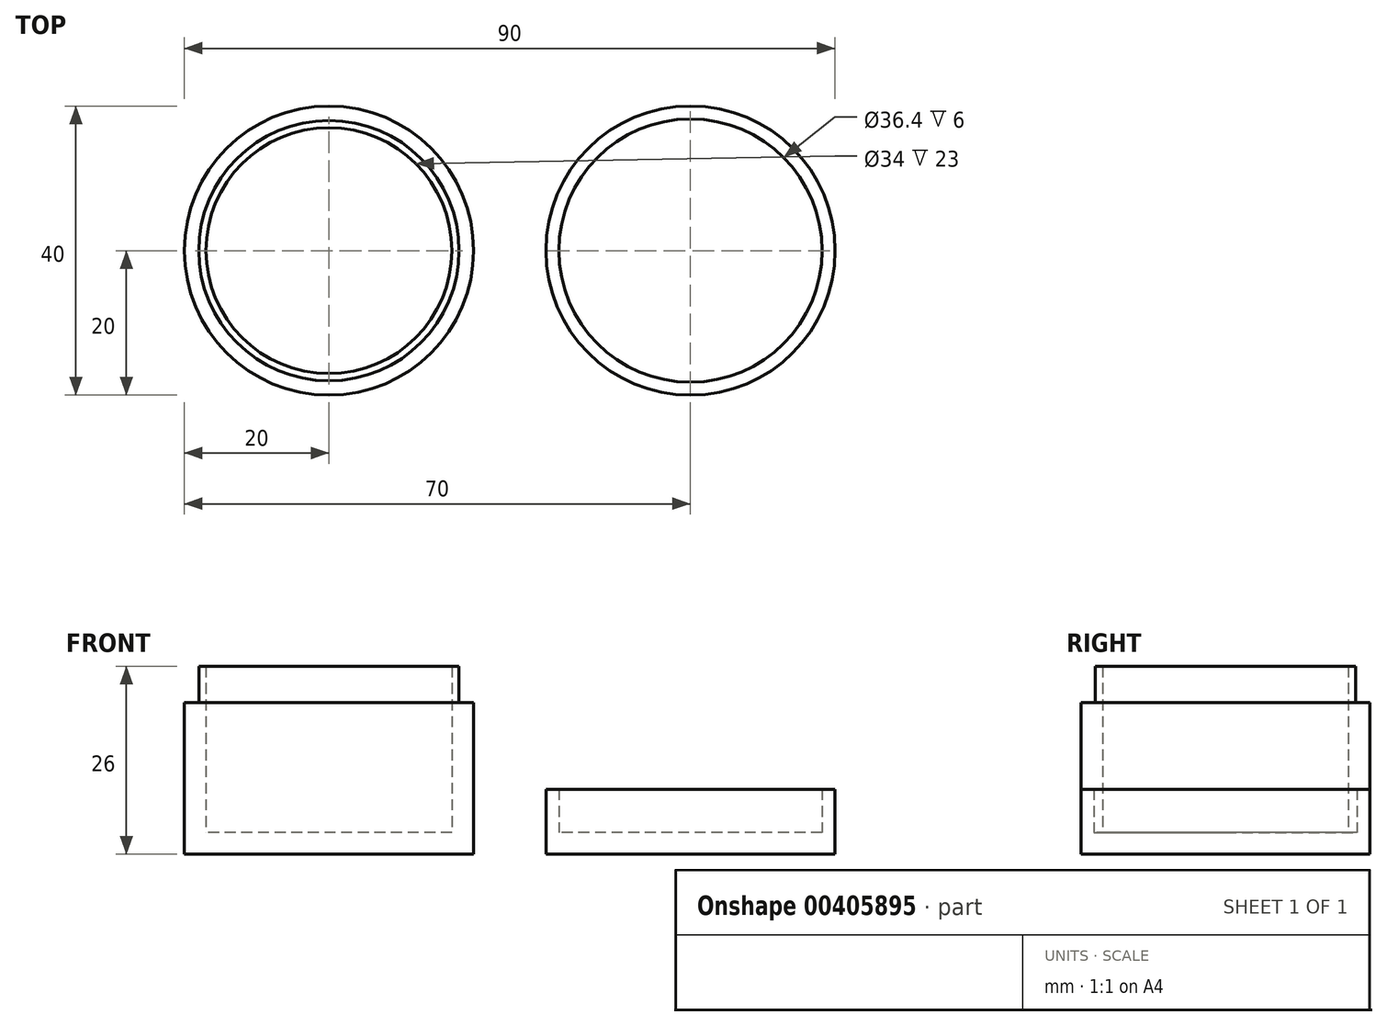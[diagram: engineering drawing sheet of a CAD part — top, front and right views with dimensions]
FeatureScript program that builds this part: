
annotation { "Feature Type Name" : "Feature", "Feature Type Description" : "" }
export const myFeature = defineFeature(function(context is Context, id is Id, definition is map)
    precondition{}
    {
        {
            assignVariable(context, id + "F0", {"name" : "base_height", "anyValue" : 21});
        }
        {
            assignVariable(context, id + "F1", {"name" : "top_height", "anyValue" : 9});
        }
        {
            assignVariable(context, id + "F2", {"name" : "rim_height", "anyValue" : 5});
        }
        {
            var Q0;
            Q0=qCreatedBy(makeId("Top.planeOp"),FACE);
            var sketch = newSketch(context, id + "F3", { "sketchPlane" : qUnion([Q0])});
            skCircle(sketch, "E0", {"center": v(0, 0) * mm, "radius": 20 * mm});
            skCircle(sketch, "E1.0", {"center": v(0, 0) * mm, "radius": 18 * mm});
            skCircle(sketch, "E2.0", {"center": v(0, 0) * mm, "radius": 17 * mm});
            skSolve(sketch);
        }
        {
            var Q0;
            Q0=makeQuery(id+"F3.imprint","IMPRINT",FACE,{"disambiguationData":[TD([[makeQuery(id+"F3.imprint","IMPRINT",EDGE,{"derivedFrom":sQuery(id+"F3.wireOp",EDGE,"E2.0")}),1.0]])]});
            extrude(context, id + "F4", {"entities" : qUnion([Q0]), "depth" : 3 * mm});
        }
        {
            var Q0;
            Q0=makeQuery(id+"F3.imprint","IMPRINT",FACE,{"disambiguationData":[TD([[makeQuery(id+"F3.imprint","IMPRINT",EDGE,{"derivedFrom":sQuery(id+"F3.wireOp",EDGE,"E1.0")}),1.0]])]});
            extrude(context, id + "F5", {"entities" : qUnion([Q0]), "operationType" : NewBodyOperationType.ADD, "depth" : (getVariable(context, 'base_height') + getVariable(context, 'rim_height')) * mm});
        }
        {
            var Q0;
            Q0=makeQuery(id+"F3.imprint","IMPRINT",FACE,{"disambiguationData":[TD([[makeQuery(id+"F3.imprint","IMPRINT",EDGE,{"derivedFrom":sQuery(id+"F3.wireOp",EDGE,"E0")}),1.0]])]});
            var Q1;
            Q1=sQuery(id+"F3.wireOp",EDGE,"E0");
            extrude(context, id + "F6", {"entities" : qUnion([Q0]), "operationType" : NewBodyOperationType.ADD, "surfaceEntities" : qUnion([Q1]), "depth" : (getVariable(context, 'base_height')) * mm});
        }
        {
            var Q0;
            Q0=qCreatedBy(makeId("Top.planeOp"),FACE);
            var sketch = newSketch(context, id + "F7", { "sketchPlane" : qUnion([Q0])});
            skCircle(sketch, "E3", {"center": v(50, 0) * mm, "radius": 20 * mm});
            skCircle(sketch, "E4.0", {"center": v(50, 0) * mm, "radius": 18.2 * mm});
            skSolve(sketch);
        }
        {
            var Q0;
            Q0=makeQuery(id+"F7.imprint","IMPRINT",FACE,{"disambiguationData":[TD([[makeQuery(id+"F7.imprint","IMPRINT",EDGE,{"derivedFrom":sQuery(id+"F7.wireOp",EDGE,"E4.0")}),1.0]])]});
            extrude(context, id + "F8", {"entities" : qUnion([Q0]), "depth" : 3 * mm});
        }
        {
            var Q0;
            Q0=makeQuery(id+"F7.imprint","IMPRINT",FACE,{"disambiguationData":[TD([[makeQuery(id+"F7.imprint","IMPRINT",EDGE,{"derivedFrom":sQuery(id+"F7.wireOp",EDGE,"E3")}),1.0]])]});
            extrude(context, id + "F9", {"entities" : qUnion([Q0]), "operationType" : NewBodyOperationType.ADD, "depth" : (getVariable(context, 'top_height')) * mm});
        }
    });
